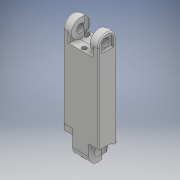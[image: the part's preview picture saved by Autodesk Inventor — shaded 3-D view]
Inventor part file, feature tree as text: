
AUTODESK INVENTOR PART (.ipt)
format: ipt  version: 2018 (Build 220112000, 112)  size: 432,640 bytes
history: native  units: mm
features: extrude x16, sketch x16, fillet x2, other x1
ambient origin geometry x8: Origin, YZ Plane, XZ Plane, XY Plane, X Axis, Y Axis, Z Axis, Center Point
bodies: Body1 (feature_tree)
feature tree (35):
  other  "Sólido1"
  extrude  "Extrusión1"  Depth=70.0mm
  extrude  "Extrusión2"  Depth=10.0mm TaperAngle=0.0deg
  extrude  "Extrusión3"  Depth=9.0mm
  sketch  "Boceto4"  dims[d7=21.0mm d8=0.0mm d9=8.0mm]
  extrude  "Extrusión4"  Depth=8.0mm
  extrude  "Extrusión5"  Depth=18.0mm TaperAngle=0.0deg
  extrude  "Extrusión6"  Depth=2.0mm
  extrude  "Extrusión7"  Depth=5.0mm
  extrude  "Extrusión8"  Depth=2.0mm
  extrude  "Extrusión9"  Depth=2.0mm TaperAngle=0.0deg
  extrude  "Extrusión10"  Depth=3.0mm
  extrude  "Extrusión11"  Depth=4.0mm
  extrude  "Extrusión12"  Depth=4.0mm
  fillet  "Empalme1"  Radius=80.0mm
  extrude  "Extrusión13"  Depth=7.0mm
  extrude  "Extrusión14"  Depth=10.0mm TaperAngle=0.0deg
  fillet  "Empalme2"  Radius=10.0mm
  extrude  "Extrusión15"  Depth=2.0mm
  extrude  "Extrusión16"  Depth=2.0mm TaperAngle=0.0deg
  sketch  "Boceto1"  dims[d0=16.0mm d1=70.0mm]
  sketch  "Boceto2"  dims[d2=10.0mm d3=30.0mm d4=0.0mm]
  sketch  "Boceto3"  dims[d5=9.0mm d6=9.0mm]
  sketch  "Boceto5"  dims[d10=7.0mm d11=18.0mm d12=0.0mm]
  sketch  "Boceto6"  dims[d16=2.0mm d17=5.0mm]
  sketch  "Boceto7"  dims[d18=5.0mm d20=5.0mm]
  sketch  "Boceto8"  dims[d21=5.0mm d24=2.0mm]
  sketch  "Boceto9"  dims[d25=2.0mm d26=16.0mm d27=0.0mm]
  sketch  "Boceto10"  dims[d33=3.0mm d34=3.0mm]
  sketch  "Boceto11"  dims[d35=3.0mm d36=4.0mm]
  sketch  "Boceto12"  dims[d37=4.0mm d38=4.0mm d39=80.0mm d40=0.0mm]
  sketch  "Boceto14"  dims[d41=12.0mm d42=7.0mm]
  sketch  "Boceto15"  dims[d43=5.0mm d44=0.0mm d45=5.0mm d46=0.0mm d47=10.0mm]
  sketch  "Boceto16"  dims[d48=2.0mm d49=0.0mm d50=5.0mm]
  sketch  "Boceto17"  dims[d54=10.0mm d59=2.0mm d60=0.0mm d61=16.0mm d62=4.0mm d63=0.0mm d64=7.0mm d65=4.0mm d66=0.0mm d67=20.0mm d68=0.0mm d69=1.0mm d70=17.0mm d71=90.0deg d72=2.0mm d73=8.0mm d74=0.0mm d75=17.0mm d76=2.0mm d77=8.0mm d78=0.0mm d79=1.0mm d80=17.0mm d81=14.0mm d82=16.0mm d83=90.0deg d84=8.0mm d85=2.0mm d86=19.0mm d87=3.0mm d88=0.0mm d89=0.0mm d90=3.0mm d91=7.5mm d92=3.0mm d93=7.5mm d94=4.0mm d95=4.0mm d96=20.0mm d97=90.0mm d98=0.0mm d99=0.0mm]
